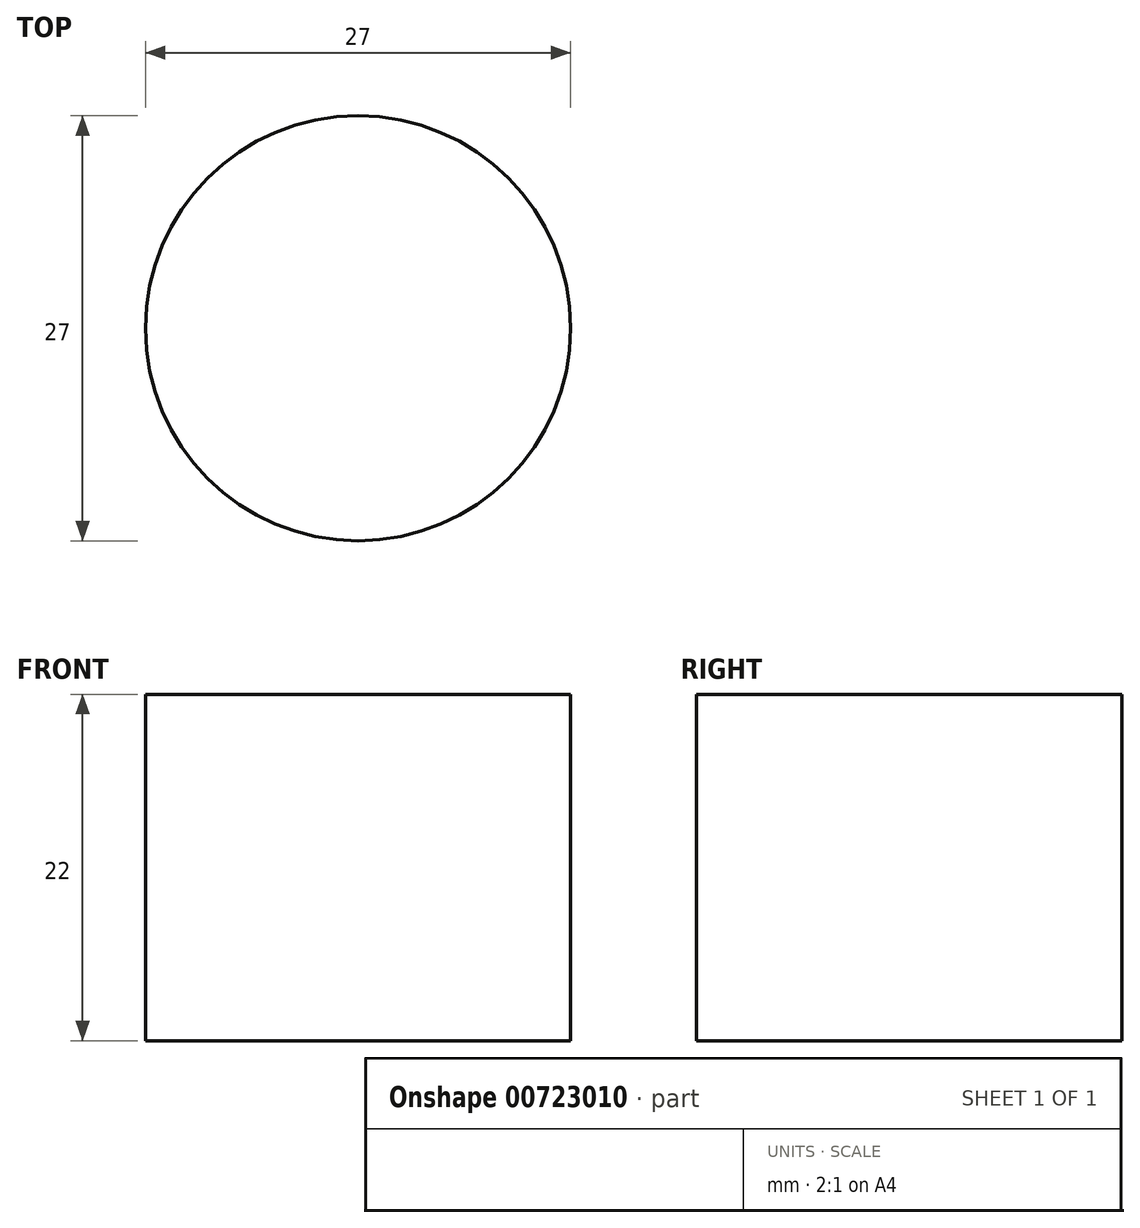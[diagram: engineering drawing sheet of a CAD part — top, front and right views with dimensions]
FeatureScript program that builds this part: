
annotation { "Feature Type Name" : "Feature", "Feature Type Description" : "" }
export const myFeature = defineFeature(function(context is Context, id is Id, definition is map)
    precondition{}
    {
        {
            var Q0;
            Q0=qCreatedBy(makeId("Top.planeOp"),FACE);
            var sketch = newSketch(context, id + "F0", { "sketchPlane" : qUnion([Q0])});
            skCircle(sketch, "E0", {"center": v(0, 0) * mm, "radius": 13.5 * mm});
            skSolve(sketch);
        }
        {
            var Q0;
            Q0=makeQuery(id+"F0.imprint","IMPRINT",FACE,{"disambiguationData":[TD([[makeQuery(id+"F0.imprint","IMPRINT",EDGE,{"derivedFrom":sQuery(id+"F0.wireOp",EDGE,"E0")}),1.0]])]});
            extrude(context, id + "F1", {"entities" : qUnion([Q0]), "depth" : 22 * mm, "offsetDistance" : 25 * mm});
        }
    });
